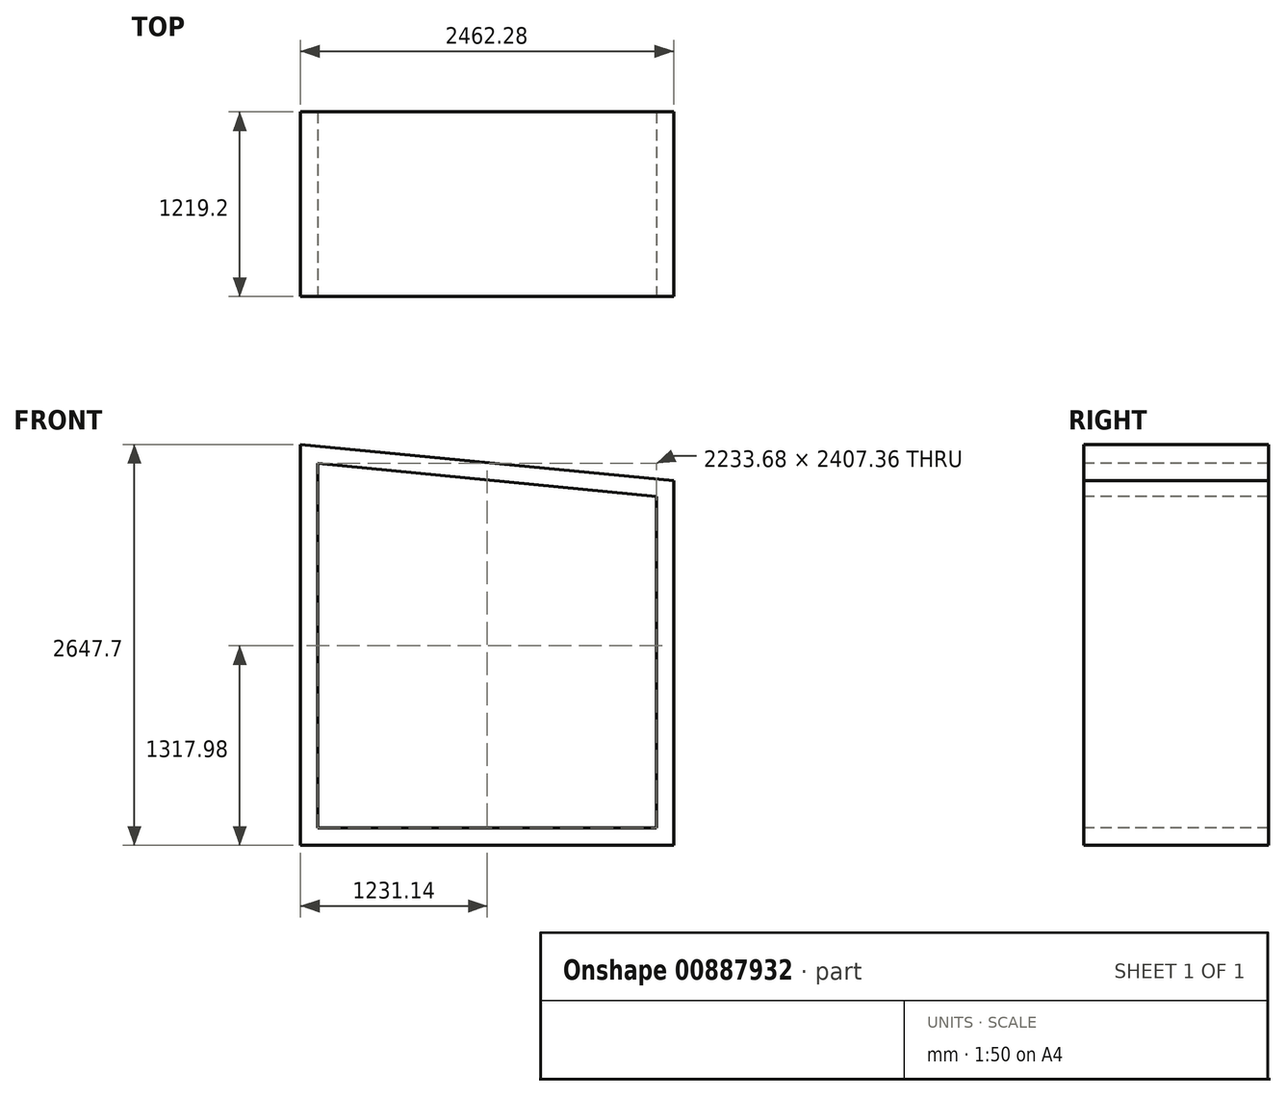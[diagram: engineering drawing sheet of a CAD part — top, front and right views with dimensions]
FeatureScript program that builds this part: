
annotation { "Feature Type Name" : "Feature", "Feature Type Description" : "" }
export const myFeature = defineFeature(function(context is Context, id is Id, definition is map)
    precondition{}
    {
        {
            var Q0;
            Q0=qCreatedBy(makeId("Front.planeOp"),FACE);
            var sketch = newSketch(context, id + "F0", { "sketchPlane" : qUnion([Q0])});
            skLineSegment(sketch, "E0", {"start": v(0, 0) * mm, "end": v(2462.28, 0) * mm});
            skLineSegment(sketch, "E1", {"start": v(2462.28, 0) * mm, "end": v(2462.28, 2406.65) * mm});
            skLineSegment(sketch, "E2", {"start": v(2462.28, 2406.65) * mm, "end": v(0, 2647.7) * mm});
            skLineSegment(sketch, "E3", {"start": v(0, 2647.7) * mm, "end": v(0, 0) * mm});
            skSolve(sketch);
        }
        {
            var Q0;
            Q0 = qSketchRegion(id + "F0", true);
            extrude(context, id + "F1", {"entities" : qUnion([Q0]), "depth" : 1219.2 * mm, "offsetDistance" : 25.4 * mm});
        }
        {
            var Q0;
            Q0=makeQuery(id+"F1.opExtrude","CAP_FACE",FACE,{"disambiguationData":[OSD([sQuery(id+"F0.wireOp",EDGE,"E0"),sQuery(id+"F0.wireOp",EDGE,"E1"),sQuery(id+"F0.wireOp",EDGE,"E2"),sQuery(id+"F0.wireOp",EDGE,"E3")])],"isStart":false});
            var sketch = newSketch(context, id + "F2", { "sketchPlane" : qUnion([Q0])});
            skLineSegment(sketch, "E4.0", {"start": v(2347.98, 2303) * mm, "end": v(114.3, 2521.66) * mm});
            skLineSegment(sketch, "E4.1", {"start": v(2347.98, 114.3) * mm, "end": v(2347.98, 2303) * mm});
            skLineSegment(sketch, "E4.2", {"start": v(114.3, 114.3) * mm, "end": v(2347.98, 114.3) * mm});
            skLineSegment(sketch, "E4.3", {"start": v(114.3, 2521.66) * mm, "end": v(114.3, 114.3) * mm});
            skSolve(sketch);
        }
        {
            var Q0;
            Q0 = qSketchRegion(id + "F2", true);
            extrude(context, id + "F3", {"entities" : qUnion([Q0]), "operationType" : NewBodyOperationType.REMOVE, "endBound" : BoundingType.THROUGH_ALL, "oppositeDirection" : true, "depth" : 25.4 * mm, "offsetDistance" : 25.4 * mm});
        }
    });
